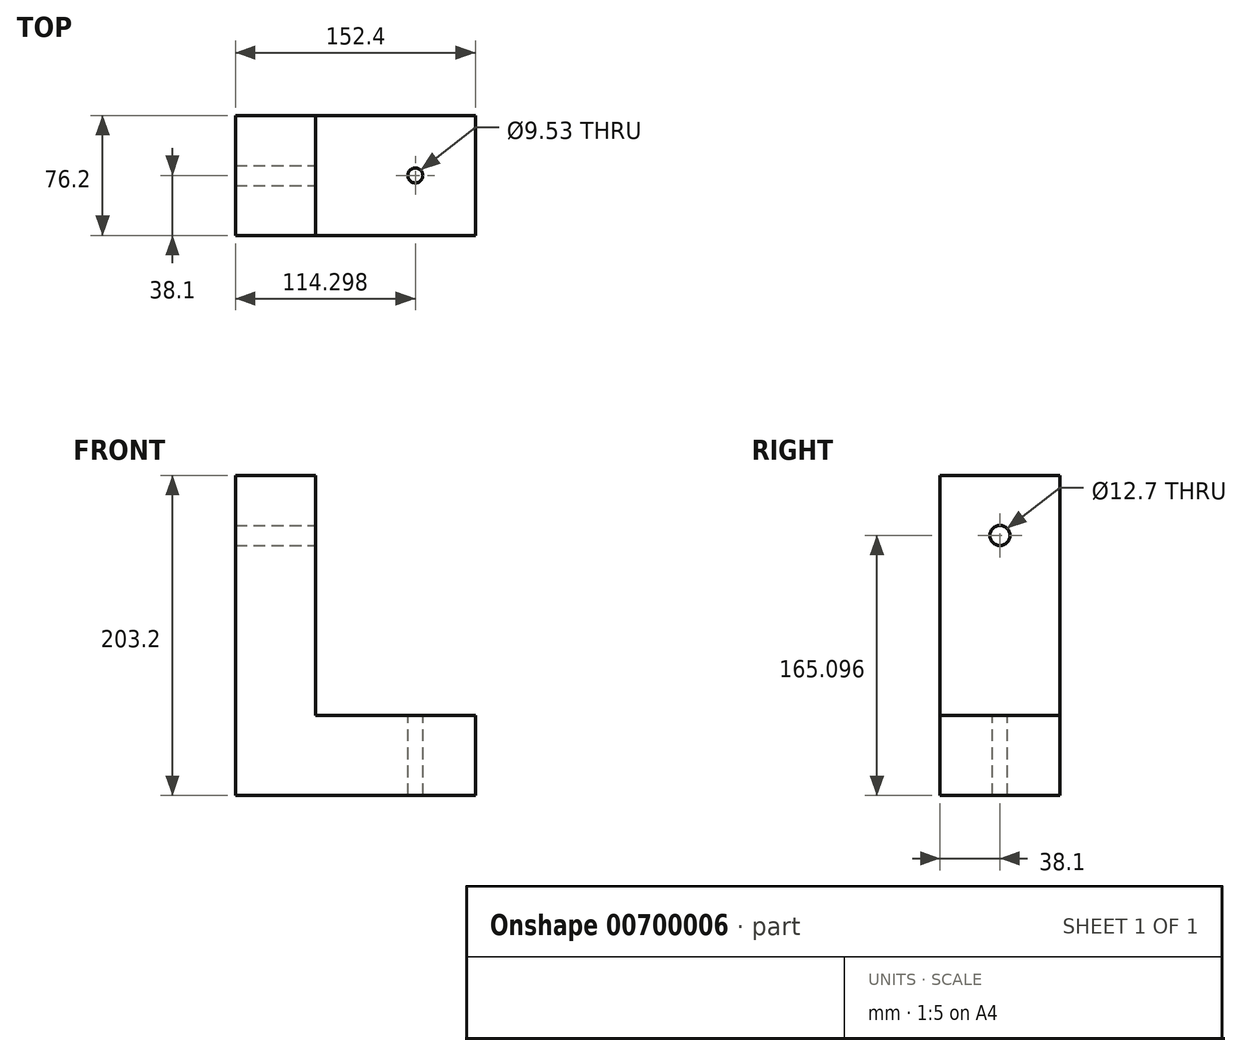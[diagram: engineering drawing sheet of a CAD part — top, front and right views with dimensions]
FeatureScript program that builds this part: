
annotation { "Feature Type Name" : "Feature", "Feature Type Description" : "" }
export const myFeature = defineFeature(function(context is Context, id is Id, definition is map)
    precondition{}
    {
        {
            var Q0;
            Q0=qCreatedBy(makeId("Front.planeOp"),FACE);
            var sketch = newSketch(context, id + "F0", { "sketchPlane" : qUnion([Q0])});
            skLineSegment(sketch, "E0", {"start": v(-71.21, 74.69) * mm, "end": v(-71.21, -128.51) * mm});
            skLineSegment(sketch, "E1", {"start": v(-71.21, -128.51) * mm, "end": v(81.19, -128.51) * mm});
            skLineSegment(sketch, "E2", {"start": v(81.19, -128.51) * mm, "end": v(81.19, -77.71) * mm});
            skLineSegment(sketch, "E3", {"start": v(81.19, -77.71) * mm, "end": v(-20.41, -77.71) * mm});
            skLineSegment(sketch, "E4", {"start": v(-20.41, -77.71) * mm, "end": v(-20.41, 74.69) * mm});
            skLineSegment(sketch, "E5", {"start": v(-20.41, 74.69) * mm, "end": v(-71.21, 74.69) * mm});
            skSolve(sketch);
        }
        {
            var Q0;
            Q0=makeQuery(id+"F0.imprint","IMPRINT",FACE,{"disambiguationData":[TD([[makeQuery(id+"F0.imprint","IMPRINT",EDGE,{"derivedFrom":sQuery(id+"F0.wireOp",EDGE,"E0")}),1.0]])]});
            extrude(context, id + "F1", {"entities" : qUnion([Q0]), "depth" : 76.2 * mm, "offsetDistance" : 25.4 * mm});
        }
        {
            var Q0;
            Q0=makeQuery(id+"F1.opExtrude","SWEPT_FACE",FACE,{"disambiguationData":[OSD([sQuery(id+"F0.wireOp",EDGE,"E3")])]});
            var sketch = newSketch(context, id + "F2", { "sketchPlane" : qUnion([Q0])});
            skCircle(sketch, "E6", {"center": v(43.09, -38.1) * mm, "radius": 4.76 * mm});
            skSolve(sketch);
        }
        {
            var Q0;
            Q0=sQuery(id+"F2.wireOp",VERTEX,"E6.center");
            var Q1;
            Q1=makeQuery(id+"F1.opExtrude","SWEPT_BODY",BODY,{"disambiguationData":[OSD([sQuery(id+"F0.wireOp",EDGE,"E0"),sQuery(id+"F0.wireOp",EDGE,"E1"),sQuery(id+"F0.wireOp",EDGE,"E2"),sQuery(id+"F0.wireOp",EDGE,"E3"),sQuery(id+"F0.wireOp",EDGE,"E4"),sQuery(id+"F0.wireOp",EDGE,"E5")])]});
            hole(context, id + "F3", {"style" : HoleStyle.SIMPLE, "endStyle" : HoleEndStyle.THROUGH, "holeDiameter" : 9.52 * mm, "majorDiameter" : 6.35 * mm, "isTappedThrough" : true, "tappedDepth" : 12.7 * mm, "tapClearance" : 3, "locations" : qUnion([Q0]), "scope" : qUnion([Q1])});
        }
        {
            var Q0;
            Q0=makeQuery(id+"F1.opExtrude","SWEPT_FACE",FACE,{"disambiguationData":[OSD([sQuery(id+"F0.wireOp",EDGE,"E4")])]});
            var sketch = newSketch(context, id + "F4", { "sketchPlane" : qUnion([Q0])});
            skCircle(sketch, "E7", {"center": v(-38.1, 36.59) * mm, "radius": 6.35 * mm});
            skSolve(sketch);
        }
        {
            var Q0;
            Q0=sQuery(id+"F4.wireOp",VERTEX,"E7.center");
            var Q1;
            Q1=makeQuery(id+"F1.opExtrude","SWEPT_BODY",BODY,{"disambiguationData":[OSD([sQuery(id+"F0.wireOp",EDGE,"E0"),sQuery(id+"F0.wireOp",EDGE,"E1"),sQuery(id+"F0.wireOp",EDGE,"E2"),sQuery(id+"F0.wireOp",EDGE,"E3"),sQuery(id+"F0.wireOp",EDGE,"E4"),sQuery(id+"F0.wireOp",EDGE,"E5")])]});
            hole(context, id + "F5", {"style" : HoleStyle.SIMPLE, "endStyle" : HoleEndStyle.THROUGH, "holeDiameter" : 12.7 * mm, "majorDiameter" : 6.35 * mm, "isTappedThrough" : true, "tappedDepth" : 12.7 * mm, "tapClearance" : 3, "locations" : qUnion([Q0]), "scope" : qUnion([Q1])});
        }
    });
